# Revit family: 3103 Series Soffit Trim Set
name_source: partatom
category: Plumbing Fixtures
units: mm (PartAtom-declared; Revit-internal decimal feet)

## family parameters
Always vertical = Yes
Cut with Voids When Loaded = No
OmniClass Number = 23.45.00.00
OmniClass Title = Sanitary, Laundry, and Cleaning Equipment
Part Type = Normal
Room Calculation Point = No
Round Connector Dimension = Use Diameter
Shared = No
Work Plane-Based = No

## types (3) — shared parameters
CW Connection = No
HW Connection = No
Manufacturer = Aquanight Industries Ltd
URL = www.aquaknight.co.nz
Vent Connection = Yes
Waste Connection = Yes
zero-valued in all types: Default Elevation

## per-type parameters (varying)
| type | 100mm | 65mm | 80mm | Description | Diameter | Model |
| 3103.525 65x65 | No | Yes | No | Roof Drain Overflow Soffit Trim Set 65mm | 65 mm  [stored 0.213255 ft] | 3103.525 |
| 3103.625 80x80 | No | No | Yes | Roof Drain Overflow Soffit Trim Set 80mm | 80 mm | 3103.625 |
| 3103.725 100x100 | Yes | No | No | Roof Drain Overflow Soffit Trim Set 100mm | 100 mm  [stored 0.328084 ft] | 3103.725 |

note: [stored X ft] marks values corroborated as IEEE doubles in the binary element streams (Revit-internal decimal feet)

## geometry (parser evidence)
native form markers: Sweep x3
no freeform markers — native parametric forms only
